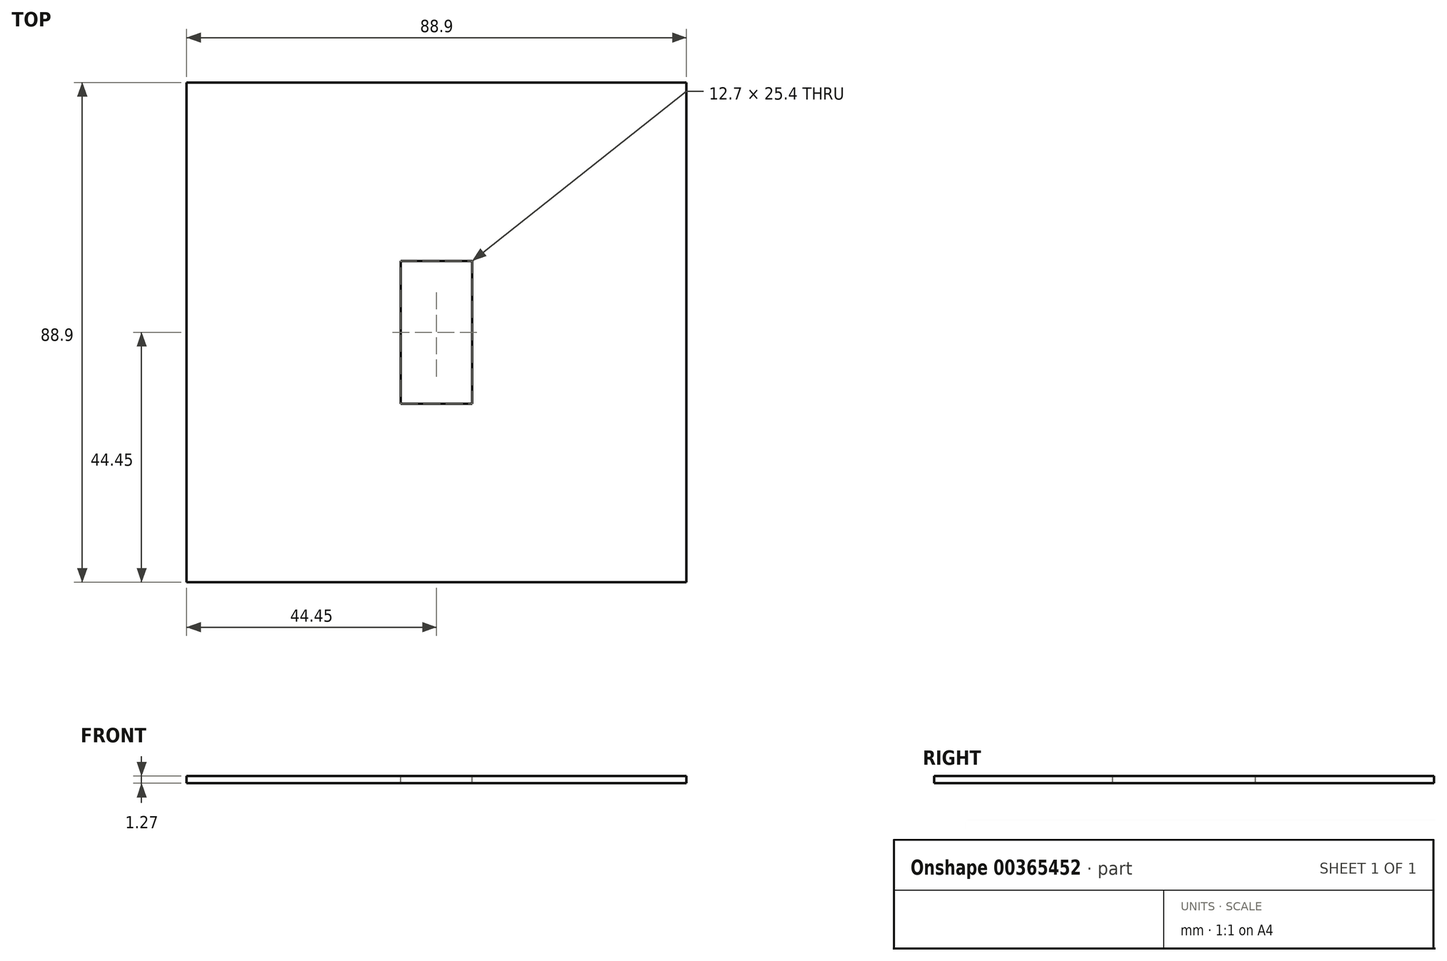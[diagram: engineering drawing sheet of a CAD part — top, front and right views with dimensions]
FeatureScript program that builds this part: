
annotation { "Feature Type Name" : "Feature", "Feature Type Description" : "" }
export const myFeature = defineFeature(function(context is Context, id is Id, definition is map)
    precondition{}
    {
        {
            var Q0;
            Q0=qCreatedBy(makeId("Top.planeOp"),FACE);
            var sketch = newSketch(context, id + "F0", { "sketchPlane" : qUnion([Q0])});
            skLineSegment(sketch, "E0.bottom", {"start": v(44.45, 44.45) * mm, "end": v(-44.45, 44.45) * mm});
            skLineSegment(sketch, "E0.top", {"start": v(44.45, -44.45) * mm, "end": v(-44.45, -44.45) * mm});
            skLineSegment(sketch, "E0.left", {"start": v(44.45, 44.45) * mm, "end": v(44.45, -44.45) * mm});
            skLineSegment(sketch, "E0.right", {"start": v(-44.45, 44.45) * mm, "end": v(-44.45, -44.45) * mm});
            skPoint(sketch, "E0.middle", {"position": v(0, 0) * mm});
            skLineSegment(sketch, "E1.bottom", {"start": v(6.35, 12.7) * mm, "end": v(-6.35, 12.7) * mm});
            skLineSegment(sketch, "E1.top", {"start": v(6.35, -12.7) * mm, "end": v(-6.35, -12.7) * mm});
            skLineSegment(sketch, "E1.left", {"start": v(6.35, 12.7) * mm, "end": v(6.35, -12.7) * mm});
            skLineSegment(sketch, "E1.right", {"start": v(-6.35, 12.7) * mm, "end": v(-6.35, -12.7) * mm});
            skSolve(sketch);
        }
        {
            var Q0;
            Q0 = qSketchRegion(id + "F0", true);
            extrude(context, id + "F1", {"entities" : qUnion([Q0]), "oppositeDirection" : true, "depth" : 1.27 * mm});
        }
    });
